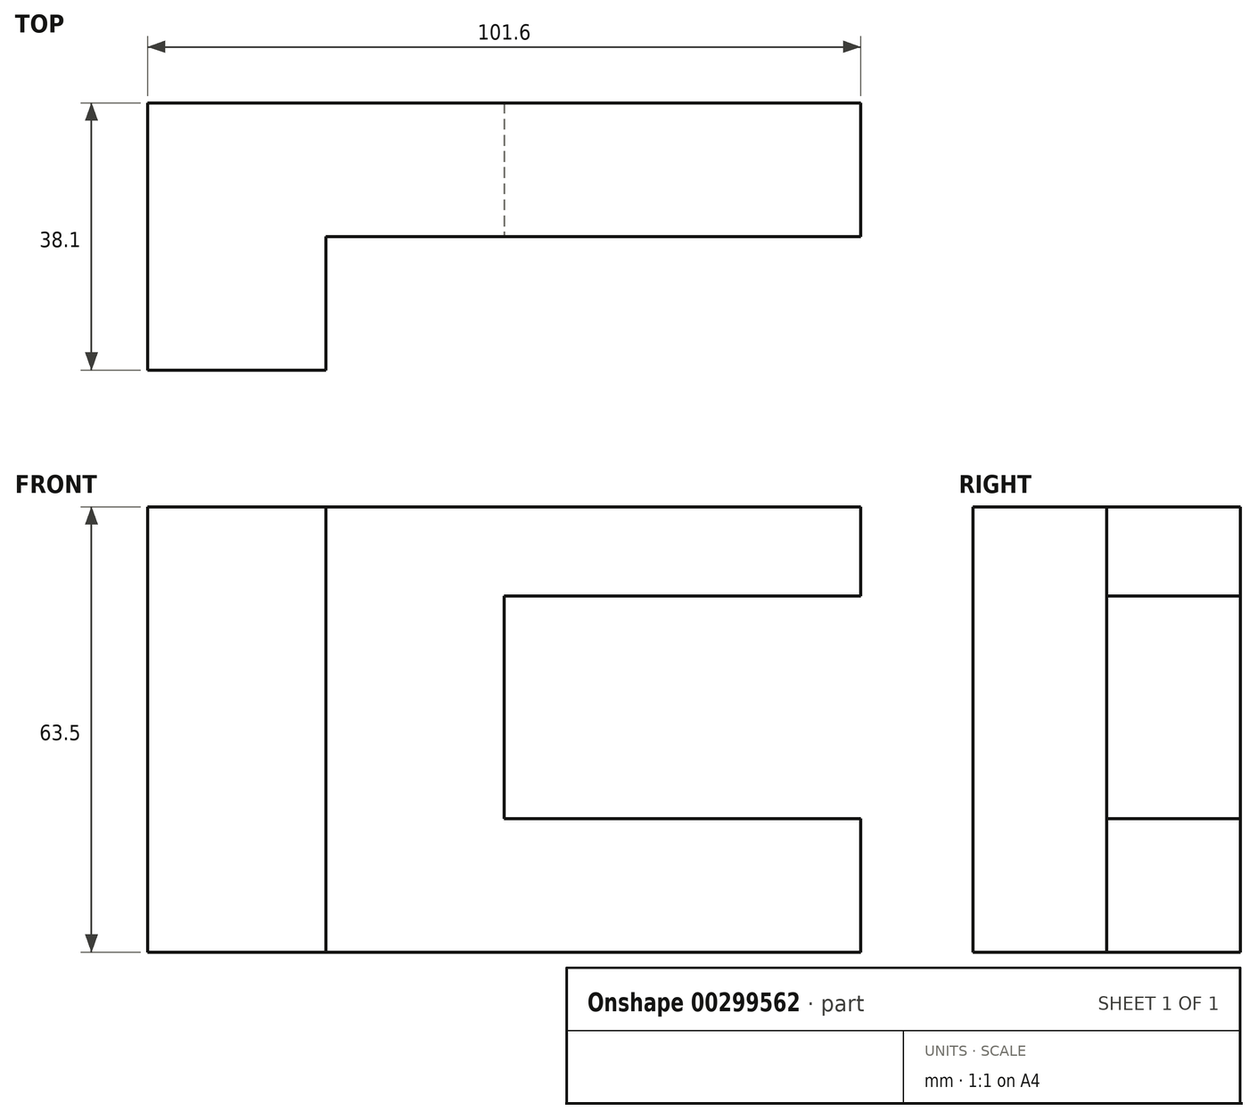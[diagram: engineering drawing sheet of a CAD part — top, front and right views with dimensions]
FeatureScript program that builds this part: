
annotation { "Feature Type Name" : "Feature", "Feature Type Description" : "" }
export const myFeature = defineFeature(function(context is Context, id is Id, definition is map)
    precondition{}
    {
        {
            var Q0;
            Q0=qCreatedBy(makeId("Front.planeOp"),FACE);
            var sketch = newSketch(context, id + "F0", { "sketchPlane" : qUnion([Q0])});
            skLineSegment(sketch, "E0.bottom", {"start": v(-50.8, 31.75) * mm, "end": v(50.8, 31.75) * mm});
            skLineSegment(sketch, "E0.top", {"start": v(-50.8, -31.75) * mm, "end": v(50.8, -31.75) * mm});
            skLineSegment(sketch, "E0.left", {"start": v(-50.8, 31.75) * mm, "end": v(-50.8, -31.75) * mm});
            skLineSegment(sketch, "E0.right", {"start": v(50.8, 31.75) * mm, "end": v(50.8, -31.75) * mm});
            skPoint(sketch, "E0.middle", {"position": v(0, 0) * mm});
            skSolve(sketch);
        }
        {
            var Q0;
            Q0 = qSketchRegion(id + "F0", true);
            extrude(context, id + "F1", {"entities" : qUnion([Q0]), "depth" : 19.05 * mm});
        }
        {
            var Q0;
            Q0=makeQuery(id+"F1.opExtrude","CAP_FACE",FACE,{"disambiguationData":[OSD([sQuery(id+"F0.wireOp",EDGE,"E0.bottom"),sQuery(id+"F0.wireOp",EDGE,"E0.top"),sQuery(id+"F0.wireOp",EDGE,"E0.left"),sQuery(id+"F0.wireOp",EDGE,"E0.right")])],"isStart":false});
            var sketch = newSketch(context, id + "F2", { "sketchPlane" : qUnion([Q0])});
            skLineSegment(sketch, "E1.bottom", {"start": v(-50.8, 31.75) * mm, "end": v(-25.4, 31.75) * mm});
            skLineSegment(sketch, "E1.top", {"start": v(-50.8, -31.75) * mm, "end": v(-25.4, -31.75) * mm});
            skLineSegment(sketch, "E1.left", {"start": v(-50.8, 31.75) * mm, "end": v(-50.8, -31.75) * mm});
            skLineSegment(sketch, "E1.right", {"start": v(-25.4, 31.75) * mm, "end": v(-25.4, -31.75) * mm});
            skSolve(sketch);
        }
        {
            var Q0;
            Q0 = qSketchRegion(id + "F2", true);
            extrude(context, id + "F3", {"entities" : qUnion([Q0]), "operationType" : NewBodyOperationType.ADD, "depth" : 19.05 * mm});
        }
        {
            var Q0;
            Q0=makeQuery(id+"F1.opExtrude","CAP_FACE",FACE,{"disambiguationData":[OSD([sQuery(id+"F0.wireOp",EDGE,"E0.bottom"),sQuery(id+"F0.wireOp",EDGE,"E0.top"),sQuery(id+"F0.wireOp",EDGE,"E0.left"),sQuery(id+"F0.wireOp",EDGE,"E0.right")])],"isStart":false});
            var sketch = newSketch(context, id + "F4", { "sketchPlane" : qUnion([Q0])});
            skLineSegment(sketch, "E2.bottom", {"start": v(50.8, 19.05) * mm, "end": v(0, 19.05) * mm});
            skLineSegment(sketch, "E2.top", {"start": v(50.8, -12.7) * mm, "end": v(0, -12.7) * mm});
            skLineSegment(sketch, "E2.left", {"start": v(50.8, 19.05) * mm, "end": v(50.8, -12.7) * mm});
            skLineSegment(sketch, "E2.right", {"start": v(0, 19.05) * mm, "end": v(0, -12.7) * mm});
            skSolve(sketch);
        }
        {
            var Q0;
            Q0 = qSketchRegion(id + "F4", true);
            extrude(context, id + "F5", {"entities" : qUnion([Q0]), "operationType" : NewBodyOperationType.REMOVE, "endBound" : BoundingType.THROUGH_ALL, "oppositeDirection" : true, "depth" : 25.4 * mm});
        }
    });
